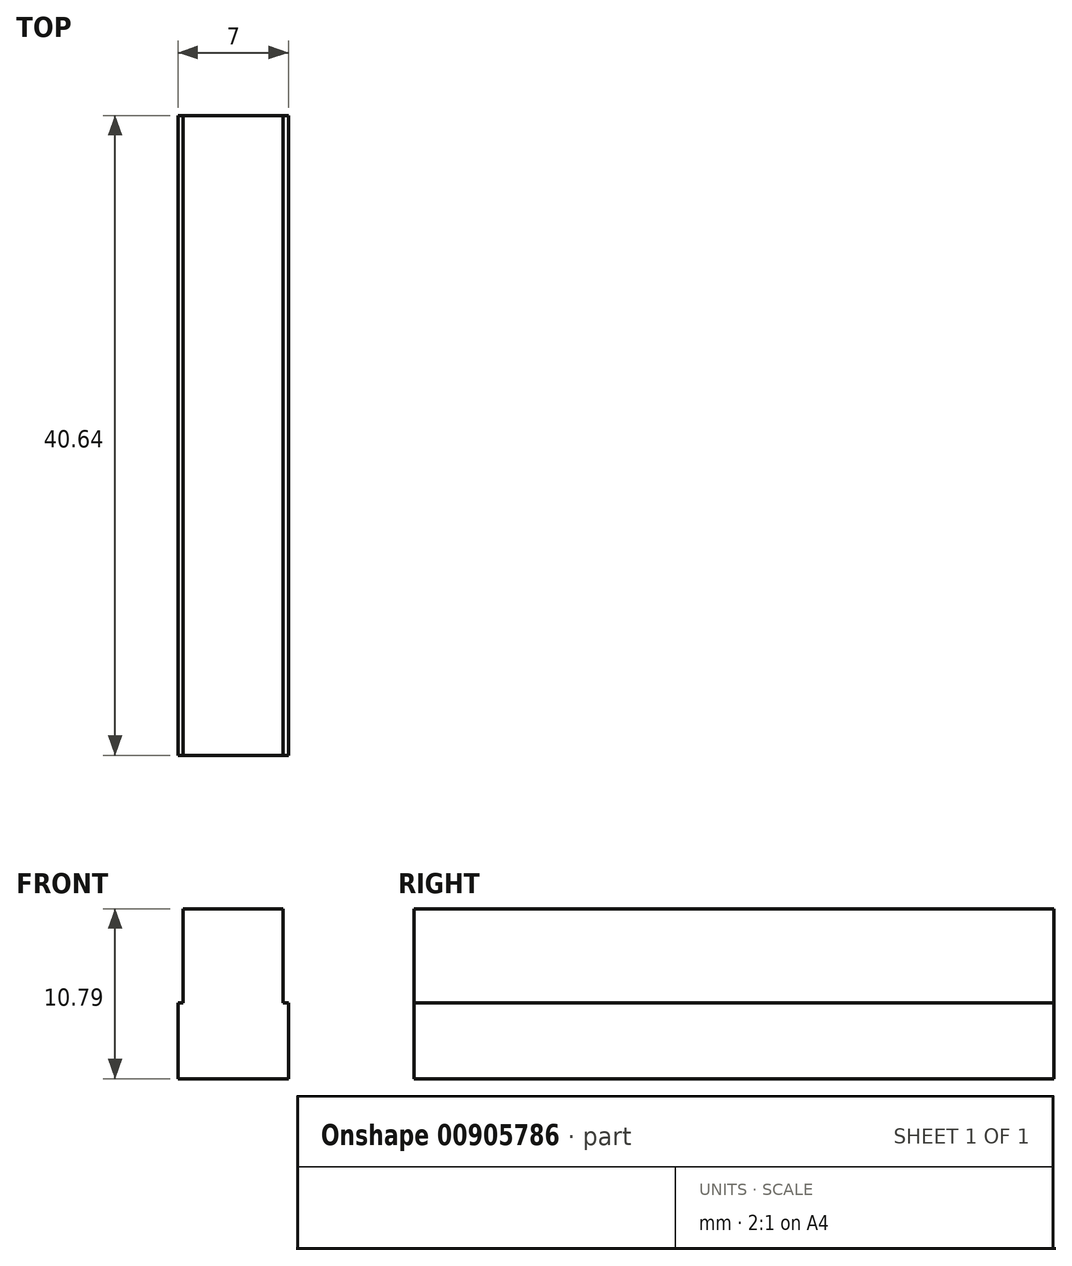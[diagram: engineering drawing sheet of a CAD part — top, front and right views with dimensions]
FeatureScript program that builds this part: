
annotation { "Feature Type Name" : "Feature", "Feature Type Description" : "" }
export const myFeature = defineFeature(function(context is Context, id is Id, definition is map)
    precondition{}
    {
        {
            var Q0;
            Q0=qCreatedBy(makeId("Front.planeOp"),FACE);
            var sketch = newSketch(context, id + "F0", { "sketchPlane" : qUnion([Q0])});
            skLineSegment(sketch, "E0.bottom", {"start": v(-3.5, 20.96) * mm, "end": v(3.5, 20.96) * mm});
            skLineSegment(sketch, "E0.top", {"start": v(-3.17, 31.75) * mm, "end": v(3.17, 31.75) * mm});
            skLineSegment(sketch, "E0.left", {"start": v(-3.5, 20.96) * mm, "end": v(-3.5, 25.78) * mm});
            skLineSegment(sketch, "E0.right", {"start": v(3.5, 20.96) * mm, "end": v(3.5, 25.78) * mm});
            skLineSegment(sketch, "E1", {"start": v(-3.17, 31.75) * mm, "end": v(-3.18, 25.78) * mm});
            skLineSegment(sketch, "E2", {"start": v(3.17, 31.75) * mm, "end": v(3.18, 25.78) * mm});
            skLineSegment(sketch, "E3", {"start": v(-3.18, 25.78) * mm, "end": v(-3.5, 25.78) * mm});
            skLineSegment(sketch, "E4", {"start": v(3.18, 25.78) * mm, "end": v(3.5, 25.78) * mm});
            skSolve(sketch);
        }
        {
            var Q0;
            Q0=makeQuery(id+"F0.imprint","IMPRINT",FACE,{"disambiguationData":[TD([[makeQuery(id+"F0.imprint","IMPRINT",EDGE,{"derivedFrom":sQuery(id+"F0.wireOp",EDGE,"E0.bottom")}),1.0]])]});
            extrude(context, id + "F1", {"entities" : qUnion([Q0]), "endBound" : BoundingType.SYMMETRIC, "depth" : 40.64 * mm, "offsetDistance" : 25.4 * mm});
        }
    });
